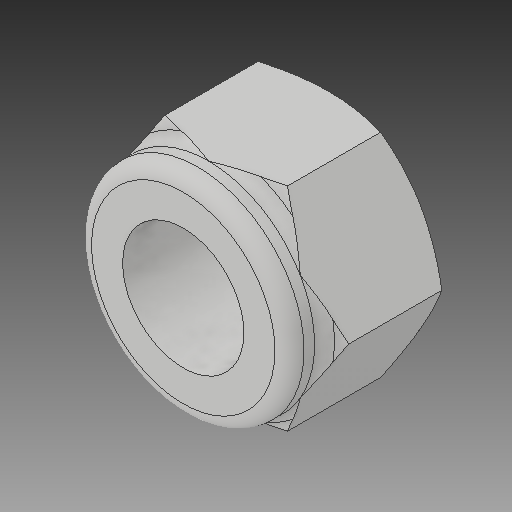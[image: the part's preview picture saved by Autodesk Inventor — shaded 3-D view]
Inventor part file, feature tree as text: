
AUTODESK INVENTOR PART (.ipt)
format: ipt  version: 2017 (Build 210142000, 142)  size: 167,936 bytes
history: native  units: in
note: dims shown in document units (in); Inventor stores cm internally (conversion verified against a paired STEP export)
features: fillet x1
ambient origin geometry x8: Origin, YZ Plane, XZ Plane, XY Plane, X Axis, Y Axis, Z Axis, Center Point
bodies: Solid1 (feature_tree)
feature tree (1):
  fillet  "Fillet7"  [1 undecoded]
note: 1 required parameter value undecoded (feature->parameter linkage not recoverable at this tier; creation-order binding heuristic only, values carry confidence <= 0.55)
